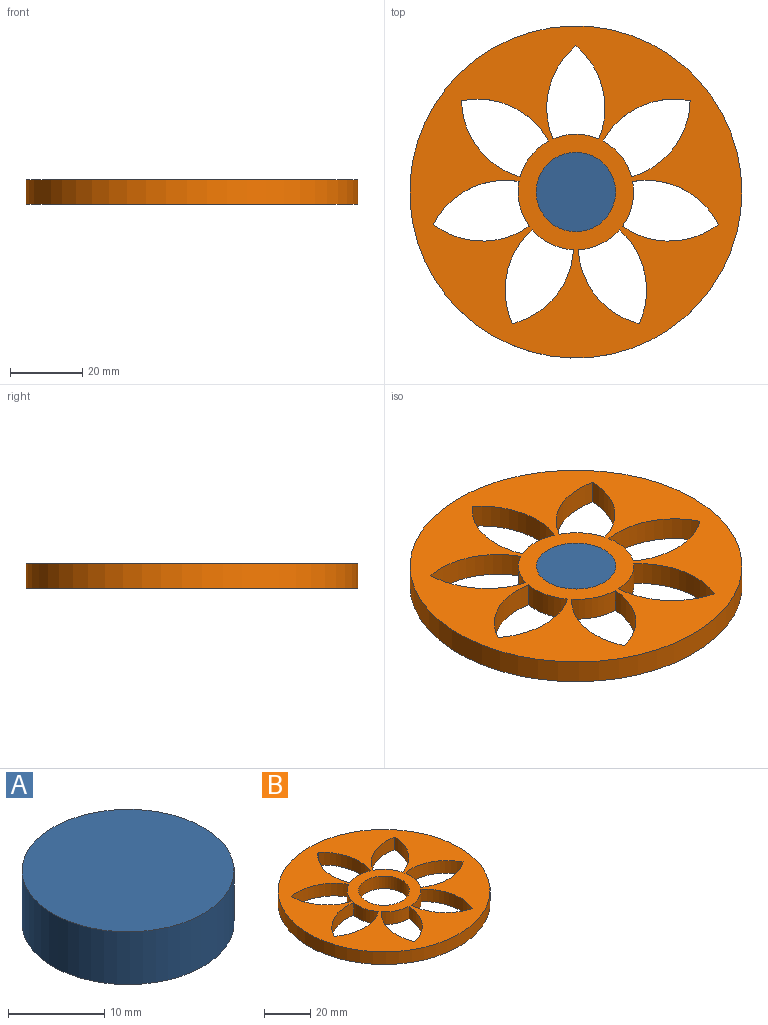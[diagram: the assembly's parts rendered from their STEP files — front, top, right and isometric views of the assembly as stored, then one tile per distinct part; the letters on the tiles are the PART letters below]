
ASSEMBLY  parts=2 mates=1
PART A: 3 faces, bbox 22x22x6.7 mm
  f0: cylinder r=11mm len=22mm, axis (0,0,-1), area 463.1mm2, adj f1,f2
  f1: plane 22x22mm, normal (0,0,1), area 380.1mm2, adj f0
  f2: plane 22x22mm, normal (0,0,-1), area 380.1mm2, adj f0
PART B: 25 faces, bbox 92x92x6.7 mm
  f0: cylinder r=16mm len=9.92mm, axis (0,0,-1), area 87.4mm2, adj f1,f15,f23,f24
  f1: cylinder r=22.37mm len=21.06mm, axis (0,0,-1), area 190.7mm2, adj f0,f15,f23,f24
  f2: cylinder r=22.37mm len=23.76mm, axis (0,0,-1), area 190.7mm2, adj f3,f16,f23,f24
  f3: cylinder r=16mm len=12.37mm, axis (0,0,-1), area 87.4mm2, adj f2,f16,f23,f24
  f4: cylinder r=22.37mm len=26.01mm, axis (0,0,-1), area 190.7mm2, adj f5,f17,f23,f24
  f5: cylinder r=16mm len=11.43mm, axis (0,0,-1), area 87.4mm2, adj f4,f17,f23,f24
  f6: cylinder r=22.37mm len=20.51mm, axis (0,0,-1), area 190.7mm2, adj f7,f18,f23,f24
  f7: cylinder r=16mm len=11.43mm, axis (0,0,-1), area 87.4mm2, adj f6,f18,f23,f24
  f8: cylinder r=22.37mm len=26.58mm, axis (0,0,-1), area 190.7mm2, adj f9,f19,f23,f24
  f9: cylinder r=16mm len=12.37mm, axis (0,0,-1), area 87.4mm2, adj f8,f19,f23,f24
  f10: cylinder r=22.37mm len=21.06mm, axis (0,0,-1), area 190.7mm2, adj f11,f20,f23,f24
  f11: cylinder r=16mm len=9.92mm, axis (0,0,-1), area 87.4mm2, adj f10,f20,f23,f24
  f12: cylinder r=22.37mm len=25.81mm, axis (0,0,-1), area 190.7mm2, adj f13,f21,f23,f24
  f13: cylinder r=16mm len=12.69mm, axis (0,0,-1), area 87.4mm2, adj f12,f21,f23,f24
  f14: cylinder r=46mm len=92mm, axis (0,0,-1), area 1936.5mm2, adj f23,f24
  f15: cylinder r=22.37mm len=24.14mm, axis (0,0,-1), area 190.7mm2, adj f0,f1,f23,f24
  f16: cylinder r=22.37mm len=26.58mm, axis (0,0,-1), area 190.7mm2, adj f2,f3,f23,f24
  f17: cylinder r=22.37mm len=20.51mm, axis (0,0,-1), area 190.7mm2, adj f4,f5,f23,f24
  f18: cylinder r=22.37mm len=26.01mm, axis (0,0,-1), area 190.7mm2, adj f6,f7,f23,f24
  f19: cylinder r=22.37mm len=23.76mm, axis (0,0,-1), area 190.7mm2, adj f8,f9,f23,f24
  f20: cylinder r=22.37mm len=24.14mm, axis (0,0,-1), area 190.7mm2, adj f10,f11,f23,f24
  f21: cylinder r=22.37mm len=25.81mm, axis (0,0,-1), area 190.7mm2, adj f12,f13,f23,f24
  f22: cylinder r=11mm len=22mm, axis (0,0,-1), area 463.1mm2, adj f23,f24
  f23: plane 92x92mm, normal (0,0,1), area 4090.2mm2, adj f0,f1,f2,f3,f4,f5,f6,f7
  f24: plane 92x92mm, normal (0,0,-1), area 4090.2mm2, adj f0,f1,f2,f3,f4,f5,f6,f7
PLACE A t=(-32.83,-9.63,16.47)mm
PLACE B t=(-32.83,-9.63,16.47)mm
MATE revolute B.f22 <-> A.f0  axis (0,0,-1) through (-32.83,-9.63,16.47)mm
